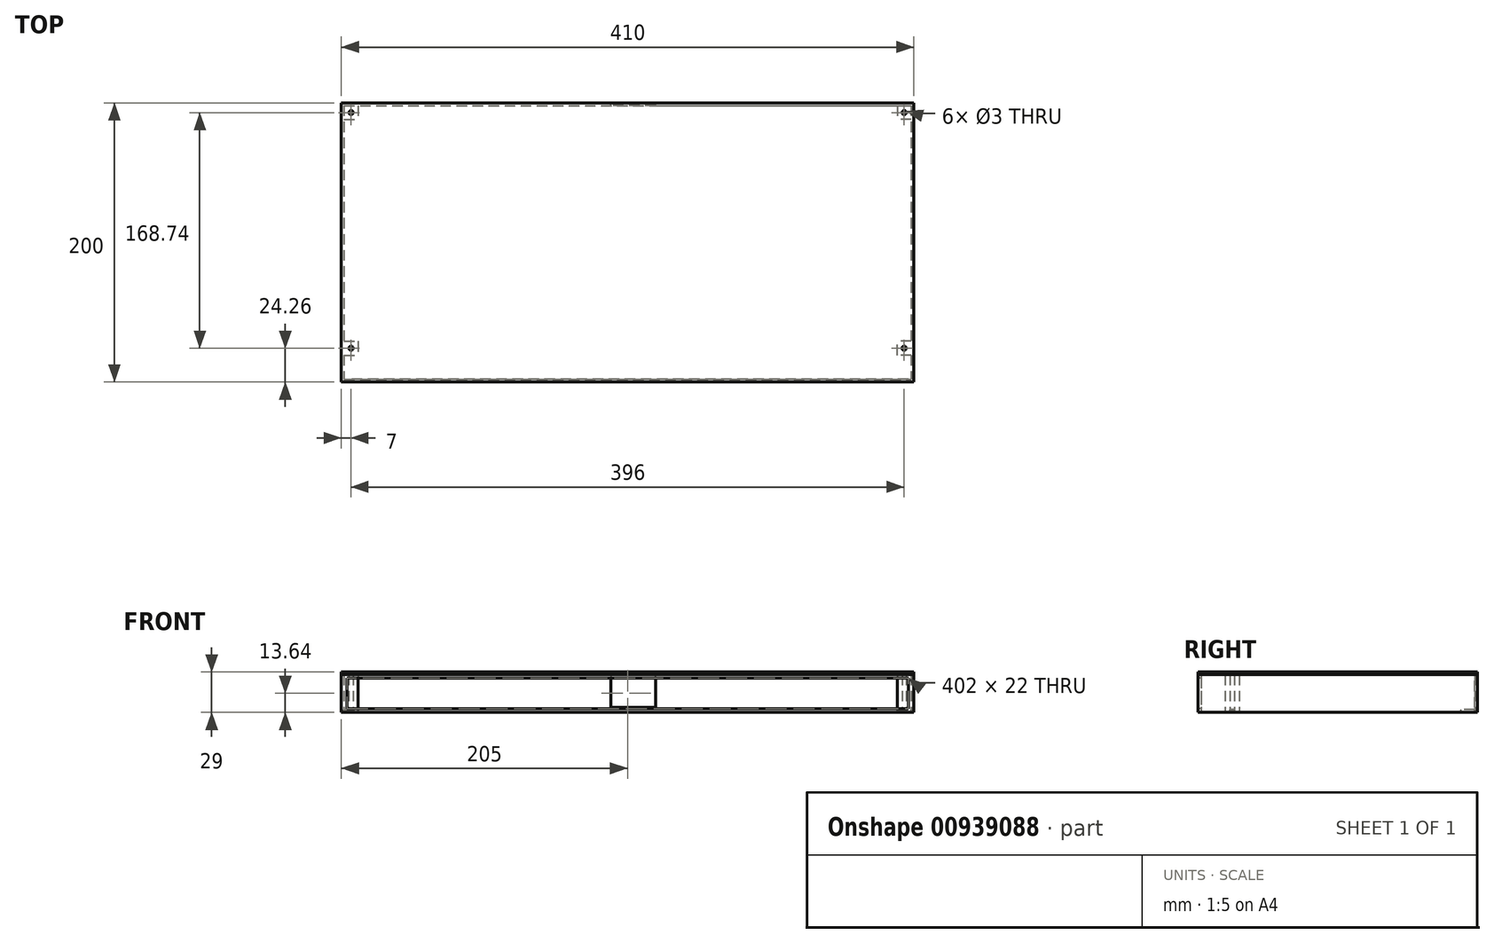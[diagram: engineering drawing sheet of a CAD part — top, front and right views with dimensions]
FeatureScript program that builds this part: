
annotation { "Feature Type Name" : "Feature", "Feature Type Description" : "" }
export const myFeature = defineFeature(function(context is Context, id is Id, definition is map)
    precondition{}
    {
        {
            var Q0;
            Q0=qCreatedBy(makeId("Top.planeOp"),FACE);
            var sketch = newSketch(context, id + "F0", { "sketchPlane" : qUnion([Q0])});
            skLineSegment(sketch, "E0.bottom", {"start": v(-205, -100) * mm, "end": v(205, -100) * mm});
            skLineSegment(sketch, "E0.top", {"start": v(-205, 100) * mm, "end": v(205, 100) * mm});
            skLineSegment(sketch, "E0.left", {"start": v(-205, -100) * mm, "end": v(-205, 100) * mm});
            skLineSegment(sketch, "E0.right", {"start": v(205, -100) * mm, "end": v(205, 100) * mm});
            skPoint(sketch, "E0.middle", {"position": v(0, 0) * mm});
            skLineSegment(sketch, "E1.bottom", {"start": v(-203, 98) * mm, "end": v(203, 98) * mm});
            skLineSegment(sketch, "E1.top", {"start": v(-203, -98) * mm, "end": v(203, -98) * mm});
            skLineSegment(sketch, "E1.left", {"start": v(-203, 98) * mm, "end": v(-203, -98) * mm});
            skLineSegment(sketch, "E1.right", {"start": v(203, 98) * mm, "end": v(203, -98) * mm});
            skLineSegment(sketch, "E2.bottom", {"start": v(-203, 98) * mm, "end": v(-193, 98) * mm});
            skLineSegment(sketch, "E2.top", {"start": v(-203, 88) * mm, "end": v(-193, 88) * mm});
            skLineSegment(sketch, "E2.left", {"start": v(-203, 98) * mm, "end": v(-203, 88) * mm});
            skLineSegment(sketch, "E2.right", {"start": v(-193, 98) * mm, "end": v(-193, 88) * mm});
            skLineSegment(sketch, "E3.bottom", {"start": v(203, 98) * mm, "end": v(193, 98) * mm});
            skLineSegment(sketch, "E3.top", {"start": v(203, 88) * mm, "end": v(193, 88) * mm});
            skLineSegment(sketch, "E3.left", {"start": v(203, 98) * mm, "end": v(203, 88) * mm});
            skLineSegment(sketch, "E3.right", {"start": v(193, 98) * mm, "end": v(193, 88) * mm});
            skLineSegment(sketch, "E4.bottom", {"start": v(-203, -70.74) * mm, "end": v(-193, -70.74) * mm});
            skLineSegment(sketch, "E4.top", {"start": v(-203, -80.74) * mm, "end": v(-193, -80.74) * mm});
            skLineSegment(sketch, "E4.left", {"start": v(-203, -70.74) * mm, "end": v(-203, -80.74) * mm});
            skLineSegment(sketch, "E4.right", {"start": v(-193, -70.74) * mm, "end": v(-193, -80.74) * mm});
            skLineSegment(sketch, "E5.bottom", {"start": v(203, -80.74) * mm, "end": v(193, -80.74) * mm});
            skLineSegment(sketch, "E5.top", {"start": v(203, -70.74) * mm, "end": v(193, -70.74) * mm});
            skLineSegment(sketch, "E5.left", {"start": v(203, -80.74) * mm, "end": v(203, -70.74) * mm});
            skLineSegment(sketch, "E5.right", {"start": v(193, -80.74) * mm, "end": v(193, -70.74) * mm});
            skCircle(sketch, "E6", {"center": v(-198, -75.74) * mm, "radius": 1.5 * mm});
            skCircle(sketch, "E7", {"center": v(198, -75.74) * mm, "radius": 1.5 * mm});
            skCircle(sketch, "E8", {"center": v(198, 93) * mm, "radius": 1.5 * mm});
            skCircle(sketch, "E9", {"center": v(-198, 93) * mm, "radius": 1.5 * mm});
            skSolve(sketch);
        }
        {
            var Q0;
            Q0 = qSketchRegion(id + "F0", true);
            var Q1;
            Q1=makeQuery(id+"F0.imprint","IMPRINT",FACE,{"disambiguationData":[TD([[makeQuery(id+"F0.imprint","IMPRINT",EDGE,{"derivedFrom":sQuery(id+"F0.wireOp",EDGE,"E2.bottom")}),-1.0]])]});
            var Q2;
            Q2=makeQuery(id+"F0.imprint","IMPRINT",FACE,{"disambiguationData":[TD([[makeQuery(id+"F0.imprint","IMPRINT",EDGE,{"derivedFrom":sQuery(id+"F0.wireOp",EDGE,"E4.bottom")}),-1.0]])]});
            var Q3;
            Q3=makeQuery(id+"F0.imprint","IMPRINT",FACE,{"disambiguationData":[TD([[makeQuery(id+"F0.imprint","IMPRINT",EDGE,{"derivedFrom":sQuery(id+"F0.wireOp",EDGE,"E5.bottom")}),-1.0]])]});
            var Q4;
            Q4=makeQuery(id+"F0.imprint","IMPRINT",FACE,{"disambiguationData":[TD([[makeQuery(id+"F0.imprint","IMPRINT",EDGE,{"derivedFrom":sQuery(id+"F0.wireOp",EDGE,"E3.bottom")}),1.0]])]});
            extrude(context, id + "F1", {"entities" : qUnion([Q0, Q1, Q2, Q3, Q4]), "depth" : 25 * mm, "offsetDistance" : 25 * mm, "hasSecondDirection" : true, "secondDirectionOppositeDirection" : true, "secondDirectionDepth" : 2 * mm});
        }
        {
            var Q0;
            Q0=makeQuery(id+"F0.imprint","IMPRINT",FACE,{"disambiguationData":[TD([[makeQuery(id+"F0.imprint","IMPRINT",EDGE,{"derivedFrom":sQuery(id+"F0.wireOp",EDGE,"E1.bottom")}),-1.0]])]});
            var Q1;
            Q1=makeQuery(id+"F0.imprint","IMPRINT",FACE,{"disambiguationData":[TD([[makeQuery(id+"F0.imprint","IMPRINT",EDGE,{"derivedFrom":sQuery(id+"F0.wireOp",EDGE,"E9")}),1.0]])]});
            var Q2;
            Q2=makeQuery(id+"F0.imprint","IMPRINT",FACE,{"disambiguationData":[TD([[makeQuery(id+"F0.imprint","IMPRINT",EDGE,{"derivedFrom":sQuery(id+"F0.wireOp",EDGE,"E6")}),1.0]])]});
            var Q3;
            Q3=makeQuery(id+"F0.imprint","IMPRINT",FACE,{"disambiguationData":[TD([[makeQuery(id+"F0.imprint","IMPRINT",EDGE,{"derivedFrom":sQuery(id+"F0.wireOp",EDGE,"E8")}),1.0]])]});
            var Q4;
            Q4=makeQuery(id+"F0.imprint","IMPRINT",FACE,{"disambiguationData":[TD([[makeQuery(id+"F0.imprint","IMPRINT",EDGE,{"derivedFrom":sQuery(id+"F0.wireOp",EDGE,"E7")}),1.0]])]});
            extrude(context, id + "F2", {"entities" : qUnion([Q0, Q1, Q2, Q3, Q4]), "oppositeDirection" : true, "depth" : 2 * mm, "offsetDistance" : 25 * mm});
        }
        {
            var Q0;
            Q0=makeQuery(id+"F1.opExtrude","CAP_FACE",FACE,{"disambiguationData":[OSD([sQuery(id+"F0.wireOp",EDGE,"E0.bottom"),sQuery(id+"F0.wireOp",EDGE,"E0.top"),sQuery(id+"F0.wireOp",EDGE,"E0.left"),sQuery(id+"F0.wireOp",EDGE,"E0.right"),sQuery(id+"F0.wireOp",EDGE,"E1.bottom"),sQuery(id+"F0.wireOp",EDGE,"E1.top"),sQuery(id+"F0.wireOp",EDGE,"E1.left"),sQuery(id+"F0.wireOp",EDGE,"E1.right"),sQuery(id+"F0.wireOp",EDGE,"E2.top"),sQuery(id+"F0.wireOp",EDGE,"E2.right"),sQuery(id+"F0.wireOp",EDGE,"E3.top"),sQuery(id+"F0.wireOp",EDGE,"E3.right"),sQuery(id+"F0.wireOp",EDGE,"E4.bottom"),sQuery(id+"F0.wireOp",EDGE,"E4.top"),sQuery(id+"F0.wireOp",EDGE,"E4.right"),sQuery(id+"F0.wireOp",EDGE,"E5.bottom"),sQuery(id+"F0.wireOp",EDGE,"E5.top"),sQuery(id+"F0.wireOp",EDGE,"E5.right"),sQuery(id+"F0.wireOp",EDGE,"E6"),sQuery(id+"F0.wireOp",EDGE,"E7"),sQuery(id+"F0.wireOp",EDGE,"E8"),sQuery(id+"F0.wireOp",EDGE,"E9")])],"isStart":false});
            var sketch = newSketch(context, id + "F3", { "sketchPlane" : qUnion([Q0])});
            skLineSegment(sketch, "E10.bottom", {"start": v(-205, -100) * mm, "end": v(205, -100) * mm});
            skLineSegment(sketch, "E10.top", {"start": v(-205, 100) * mm, "end": v(205, 100) * mm});
            skLineSegment(sketch, "E10.left", {"start": v(-205, -100) * mm, "end": v(-205, 100) * mm});
            skLineSegment(sketch, "E10.right", {"start": v(205, -100) * mm, "end": v(205, 100) * mm});
            skPoint(sketch, "E10.middle", {"position": v(0, 0) * mm});
            skCircle(sketch, "E11", {"center": v(-198, 93) * mm, "radius": 1.5 * mm});
            skCircle(sketch, "E12", {"center": v(-198, -75.74) * mm, "radius": 1.5 * mm});
            skCircle(sketch, "E13", {"center": v(198, -75.74) * mm, "radius": 1.5 * mm});
            skCircle(sketch, "E14", {"center": v(198, 93) * mm, "radius": 1.5 * mm});
            skSolve(sketch);
        }
        {
            var Q0;
            Q0=makeQuery(id+"F3.imprint","IMPRINT",FACE,{"disambiguationData":[TD([[makeQuery(id+"F3.imprint","IMPRINT",EDGE,{"derivedFrom":makeQuery(id+"F1.opExtrude","CAP_EDGE",EDGE,{"disambiguationData":[OSD([sQuery(id+"F0.wireOp",EDGE,"E1.bottom")])],"isStart":false})}),-1.0]])]});
            var Q1;
            Q1=makeQuery(id+"F3.imprint","IMPRINT",FACE,{"disambiguationData":[TD([[makeQuery(id+"F3.imprint","IMPRINT",EDGE,{"derivedFrom":sQuery(id+"F3.wireOp",EDGE,"E10.bottom")}),1.0]])]});
            extrude(context, id + "F4", {"entities" : qUnion([Q0, Q1]), "operationType" : NewBodyOperationType.ADD, "depth" : 2 * mm, "offsetDistance" : 25 * mm, "hasSecondDirection" : true, "secondDirectionOppositeDirection" : false, "secondDirectionDepth" : 0.01 * mm});
        }
        {
            var Q0;
            Q0=makeQuery(id+"F4.boolean.opBoolean","MERGE",FACE,{"derivedFrom":[makeQuery(id+"F1.opExtrude","SWEPT_FACE",FACE,{"disambiguationData":[OSD([sQuery(id+"F0.wireOp",EDGE,"E0.bottom")])]}),makeQuery(id+"F4.opExtrude","SWEPT_FACE",FACE,{"disambiguationData":[OSD([sQuery(id+"F3.wireOp",EDGE,"E10.bottom")])]})]});
            var sketch = newSketch(context, id + "F5", { "sketchPlane" : qUnion([Q0])});
            skLineSegment(sketch, "E15.bottom", {"start": v(-201, 0.64) * mm, "end": v(201, 0.64) * mm});
            skLineSegment(sketch, "E15.top", {"start": v(-201, 22.64) * mm, "end": v(201, 22.64) * mm});
            skLineSegment(sketch, "E15.left", {"start": v(-201, 0.64) * mm, "end": v(-201, 22.64) * mm});
            skLineSegment(sketch, "E15.right", {"start": v(201, 0.64) * mm, "end": v(201, 22.64) * mm});
            skPoint(sketch, "E15.middle", {"position": v(0, 5.34) * mm});
            skSolve(sketch);
        }
        {
            var Q0;
            Q0=makeQuery(id+"F5.imprint","IMPRINT",FACE,{"disambiguationData":[TD([[makeQuery(id+"F5.imprint","IMPRINT",EDGE,{"derivedFrom":sQuery(id+"F5.wireOp",EDGE,"E15.bottom")}),1.0]])]});
            extrude(context, id + "F6", {"entities" : qUnion([Q0]), "operationType" : NewBodyOperationType.REMOVE, "oppositeDirection" : true, "depth" : 6 * mm, "offsetDistance" : 25 * mm});
        }
        {
            var Q0;
            Q0=makeQuery(id+"F4.boolean.opBoolean","MERGE",FACE,{"derivedFrom":[makeQuery(id+"F1.opExtrude","SWEPT_FACE",FACE,{"disambiguationData":[OSD([sQuery(id+"F0.wireOp",EDGE,"E0.top")])]}),makeQuery(id+"F4.opExtrude","SWEPT_FACE",FACE,{"disambiguationData":[OSD([sQuery(id+"F3.wireOp",EDGE,"E10.top")])]})]});
            var sketch = newSketch(context, id + "F7", { "sketchPlane" : qUnion([Q0])});
            skLineSegment(sketch, "E16.top", {"start": v(-20, 25) * mm, "end": v(12, 25) * mm});
            skLineSegment(sketch, "E16.left", {"start": v(-20, 1.5) * mm, "end": v(-20, 25) * mm});
            skPoint(sketch, "E16.middle", {"position": v(-4, 12.67) * mm});
            skLineSegment(sketch, "E17.bottom", {"start": v(-205, 25) * mm, "end": v(205, 25) * mm});
            skLineSegment(sketch, "E17.top", {"start": v(-205, -2) * mm, "end": v(205, -2) * mm});
            skLineSegment(sketch, "E17.left", {"start": v(-205, 25) * mm, "end": v(-205, -2) * mm});
            skLineSegment(sketch, "E17.right", {"start": v(205, 25) * mm, "end": v(205, -2) * mm});
            skLineSegment(sketch, "E18", {"start": v(-20, 1.5) * mm, "end": v(12, 1.5) * mm});
            skLineSegment(sketch, "E19", {"start": v(12, 25) * mm, "end": v(12, 1.5) * mm});
            skSolve(sketch);
        }
        {
            var Q0;
            {var subQ0=sQuery(id+"F7.wireOp",EDGE,"E16.left");Q0=makeQuery(id+"F7.imprint","IMPRINT",FACE,{"disambiguationData":[TD([[makeQuery(id+"F7.imprint","IMPRINT",EDGE,{"derivedFrom":subQ0}),-1.0]])]});}
            extrude(context, id + "F8", {"entities" : qUnion([Q0]), "operationType" : NewBodyOperationType.REMOVE, "oppositeDirection" : true, "depth" : 10 * mm, "offsetDistance" : 25 * mm});
        }
    });
